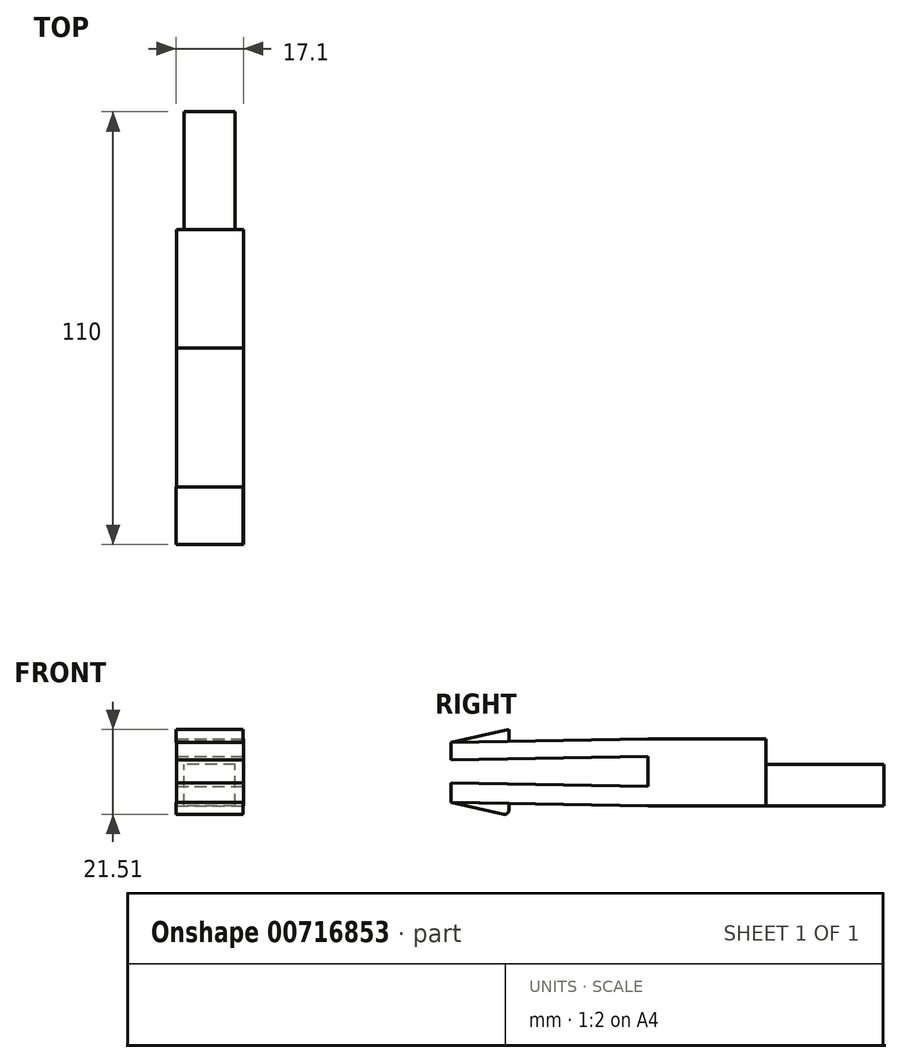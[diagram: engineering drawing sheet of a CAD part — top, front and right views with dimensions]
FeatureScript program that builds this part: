
annotation { "Feature Type Name" : "Feature", "Feature Type Description" : "" }
export const myFeature = defineFeature(function(context is Context, id is Id, definition is map)
    precondition{}
    {
        {
            var Q0;
            Q0=qCreatedBy(makeId("Front.planeOp"),FACE);
            var sketch = newSketch(context, id + "F0", { "sketchPlane" : qUnion([Q0])});
            skLineSegment(sketch, "E0.bottom", {"start": v(6.5, -5.25) * mm, "end": v(-6.5, -5.25) * mm});
            skLineSegment(sketch, "E0.top", {"start": v(6.5, 5.25) * mm, "end": v(-6.5, 5.25) * mm});
            skLineSegment(sketch, "E0.left", {"start": v(6.5, -5.25) * mm, "end": v(6.5, 5.25) * mm});
            skLineSegment(sketch, "E0.right", {"start": v(-6.5, -5.25) * mm, "end": v(-6.5, 5.25) * mm});
            skPoint(sketch, "E0.middle", {"position": v(0, 0) * mm});
            skSolve(sketch);
        }
        {
            var Q0;
            Q0 = qSketchRegion(id + "F0", true);
            extrude(context, id + "F1", {"entities" : qUnion([Q0]), "oppositeDirection" : true, "depth" : 30 * mm, "offsetDistance" : 25 * mm});
        }
        {
            var Q0;
            Q0=makeQuery(id+"F1.opExtrude","CAP_FACE",FACE,{"disambiguationData":[OSD([sQuery(id+"F0.wireOp",EDGE,"E0.bottom"),sQuery(id+"F0.wireOp",EDGE,"E0.top"),sQuery(id+"F0.wireOp",EDGE,"E0.left"),sQuery(id+"F0.wireOp",EDGE,"E0.right")])],"isStart":true});
            var sketch = newSketch(context, id + "F2", { "sketchPlane" : qUnion([Q0])});
            skLineSegment(sketch, "E1.bottom", {"start": v(-8.4, 11.75) * mm, "end": v(8.6, 11.75) * mm});
            skLineSegment(sketch, "E1.top", {"start": v(-8.4, -5.25) * mm, "end": v(8.6, -5.25) * mm});
            skLineSegment(sketch, "E1.left", {"start": v(-8.4, 11.75) * mm, "end": v(-8.4, -5.25) * mm});
            skLineSegment(sketch, "E1.right", {"start": v(8.6, 11.75) * mm, "end": v(8.6, -5.25) * mm});
            skSolve(sketch);
        }
        {
            var Q0;
            Q0=makeQuery(id+"F2.imprint","IMPRINT",FACE,{"disambiguationData":[TD([[makeQuery(id+"F2.imprint","IMPRINT",EDGE,{"derivedFrom":sQuery(id+"F2.wireOp",EDGE,"E1.bottom")}),-1.0]])]});
            var Q1;
            Q1=makeQuery(id+"F2.imprint","IMPRINT",FACE,{"disambiguationData":[TD([[makeQuery(id+"F2.imprint","IMPRINT",EDGE,{"derivedFrom":makeQuery(id+"F1.opExtrude","CAP_EDGE",EDGE,{"disambiguationData":[OSD([sQuery(id+"F0.wireOp",EDGE,"E0.top")])],"isStart":true})}),1.0]])]});
            extrude(context, id + "F3", {"entities" : qUnion([Q0, Q1]), "operationType" : NewBodyOperationType.ADD, "depth" : 30 * mm, "offsetDistance" : 25 * mm});
        }
        {
            var Q0;
            Q0=makeQuery(id+"F3.opExtrude","CAP_FACE",FACE,{"disambiguationData":[OSD([sQuery(id+"F2.wireOp",EDGE,"E1.bottom"),sQuery(id+"F2.wireOp",EDGE,"E1.top"),sQuery(id+"F2.wireOp",EDGE,"E1.left"),sQuery(id+"F2.wireOp",EDGE,"E1.right")])],"isStart":false});
            var sketch = newSketch(context, id + "F4", { "sketchPlane" : qUnion([Q0])});
            skLineSegment(sketch, "E2.bottom", {"start": v(-8.4, 11.75) * mm, "end": v(8.6, 11.75) * mm});
            skLineSegment(sketch, "E2.top", {"start": v(-8.4, 7.32) * mm, "end": v(8.6, 7.32) * mm});
            skLineSegment(sketch, "E2.left", {"start": v(-8.4, 11.75) * mm, "end": v(-8.4, 7.32) * mm});
            skLineSegment(sketch, "E2.right", {"start": v(8.6, 11.75) * mm, "end": v(8.6, 7.32) * mm});
            skLineSegment(sketch, "E3.bottom", {"start": v(-8.4, -5.25) * mm, "end": v(8.6, -5.25) * mm});
            skLineSegment(sketch, "E3.top", {"start": v(-8.4, -0.25) * mm, "end": v(8.6, -0.25) * mm});
            skLineSegment(sketch, "E3.left", {"start": v(-8.4, -5.25) * mm, "end": v(-8.4, -0.25) * mm});
            skLineSegment(sketch, "E3.right", {"start": v(8.6, -5.25) * mm, "end": v(8.6, -0.25) * mm});
            skSolve(sketch);
        }
        {
            var Q0;
            Q0=makeQuery(id+"F3.opExtrude","SWEPT_FACE",FACE,{"disambiguationData":[OSD([sQuery(id+"F2.wireOp",EDGE,"E1.right")])]});
            var sketch = newSketch(context, id + "F5", { "sketchPlane" : qUnion([Q0])});
            skLineSegment(sketch, "E4", {"start": v(-30, 9.54) * mm, "end": v(-80, 8.67) * mm});
            skLineSegment(sketch, "E5", {"start": v(-30, -2.92) * mm, "end": v(-80, -2.04) * mm});
            skSolve(sketch);
        }
        {
            var Q0;
            Q0=makeQuery(id+"F4.imprint","IMPRINT",FACE,{"disambiguationData":[TD([[makeQuery(id+"F4.imprint","IMPRINT",EDGE,{"derivedFrom":sQuery(id+"F4.wireOp",EDGE,"E2.bottom")}),-1.0]])]});
            var Q1;
            Q1=sQuery(id+"F5.wireOp",EDGE,"E4");
            sweep(context, id + "F6", {"operationType" : NewBodyOperationType.ADD, "profiles" : qUnion([Q0]), "path" : qUnion([Q1])});
        }
        {
            var Q0;
            Q0=makeQuery(id+"F4.imprint","IMPRINT",FACE,{"disambiguationData":[TD([[makeQuery(id+"F4.imprint","IMPRINT",EDGE,{"derivedFrom":sQuery(id+"F4.wireOp",EDGE,"E3.bottom")}),1.0]])]});
            var Q1;
            Q1=sQuery(id+"F5.wireOp",EDGE,"E5");
            sweep(context, id + "F7", {"operationType" : NewBodyOperationType.ADD, "profiles" : qUnion([Q0]), "path" : qUnion([Q1])});
        }
        {
            var Q0;
            Q0=qCreatedBy(makeId("Right.planeOp"),FACE);
            var sketch = newSketch(context, id + "F8", { "sketchPlane" : qUnion([Q0])});
            skLineSegment(sketch, "E6", {"start": v(-80, 10.88) * mm, "end": v(-65.35, 14.13) * mm});
            skLineSegment(sketch, "E7", {"start": v(-65.35, 14.13) * mm, "end": v(-65.35, 11.13) * mm});
            skLineSegment(sketch, "E8", {"start": v(-65.35, 11.13) * mm, "end": v(-80, 10.88) * mm});
            skLineSegment(sketch, "E9", {"start": v(-80, -4.38) * mm, "end": v(-65.35, -7.63) * mm});
            skLineSegment(sketch, "E10", {"start": v(-65.35, -7.63) * mm, "end": v(-65.35, -4.63) * mm});
            skLineSegment(sketch, "E11", {"start": v(-65.35, -4.63) * mm, "end": v(-80, -4.38) * mm});
            skSolve(sketch);
        }
        {
            var Q0;
            Q0 = qSketchRegion(id + "F8", true);
            extrude(context, id + "F9", {"entities" : qUnion([Q0]), "operationType" : NewBodyOperationType.ADD, "depth" : 8.5 * mm, "offsetDistance" : 25 * mm, "hasSecondDirection" : true, "secondDirectionOppositeDirection" : true, "secondDirectionDepth" : 8.5 * mm});
        }
        {
            var Q0;
            Q0=makeQuery(id+"F9.opExtrude","SWEPT_EDGE",EDGE,{"disambiguationData":[OSD([sQuery(id+"F8.wireOp",EDGE,"E6"),sQuery(id+"F8.wireOp",EDGE,"E7")])]});
            var Q1;
            Q1=makeQuery(id+"F9.boolean.opBoolean","MERGE",EDGE,{"derivedFrom":[makeQuery(id+"F6.opSweep","CAP_EDGE",EDGE,{"disambiguationData":[OSD([sQuery(id+"F4.wireOp",EDGE,"E2.bottom"),sQuery(id+"F5.wireOp",VERTEX,"E4.end")])],"isStart":false}),makeQuery(id+"F9.opExtrude","SWEPT_EDGE",EDGE,{"disambiguationData":[OSD([sQuery(id+"F8.wireOp",EDGE,"E6"),sQuery(id+"F8.wireOp",EDGE,"E8")])]})]});
            var Q2;
            Q2=makeQuery(id+"F3.opExtrude","CAP_EDGE",EDGE,{"disambiguationData":[OSD([sQuery(id+"F2.wireOp",EDGE,"E1.bottom")])],"isStart":true});
            var Q3;
            Q3=makeQuery(id+"F3.opExtrude","CAP_EDGE",EDGE,{"disambiguationData":[OSD([sQuery(id+"F2.wireOp",EDGE,"E1.right")])],"isStart":true});
            var Q4;
            Q4=makeQuery(id+"F3.opExtrude","CAP_EDGE",EDGE,{"disambiguationData":[OSD([sQuery(id+"F2.wireOp",EDGE,"E1.left")])],"isStart":true});
            var Q5;
            Q5=makeQuery(id+"F1.opExtrude","CAP_EDGE",EDGE,{"disambiguationData":[OSD([sQuery(id+"F0.wireOp",EDGE,"E0.right")])],"isStart":false});
            var Q6;
            Q6=makeQuery(id+"F1.opExtrude","CAP_EDGE",EDGE,{"disambiguationData":[OSD([sQuery(id+"F0.wireOp",EDGE,"E0.top")])],"isStart":false});
            var Q7;
            Q7=makeQuery(id+"F1.opExtrude","CAP_EDGE",EDGE,{"disambiguationData":[OSD([sQuery(id+"F0.wireOp",EDGE,"E0.bottom")])],"isStart":false});
            var Q8;
            Q8=makeQuery(id+"F1.opExtrude","CAP_EDGE",EDGE,{"disambiguationData":[OSD([sQuery(id+"F0.wireOp",EDGE,"E0.left")])],"isStart":false});
            var Q9;
            Q9=makeQuery(id+"F9.opExtrude","SWEPT_EDGE",EDGE,{"disambiguationData":[OSD([sQuery(id+"F8.wireOp",EDGE,"E9"),sQuery(id+"F8.wireOp",EDGE,"E10")])]});
            var Q10;
            Q10=makeQuery(id+"F9.boolean.opBoolean","MERGE",EDGE,{"derivedFrom":[makeQuery(id+"F7.opSweep","CAP_EDGE",EDGE,{"disambiguationData":[OSD([sQuery(id+"F4.wireOp",EDGE,"E3.bottom"),sQuery(id+"F5.wireOp",VERTEX,"E5.end")])],"isStart":false}),makeQuery(id+"F9.opExtrude","SWEPT_EDGE",EDGE,{"disambiguationData":[OSD([sQuery(id+"F8.wireOp",EDGE,"E9"),sQuery(id+"F8.wireOp",EDGE,"E11")])]})]});
            var Q11;
            Q11=makeQuery(id+"F6.opSweep","CAP_EDGE",EDGE,{"disambiguationData":[OSD([sQuery(id+"F4.wireOp",EDGE,"E2.top"),sQuery(id+"F5.wireOp",VERTEX,"E4.end")])],"isStart":false});
            var Q12;
            Q12=makeQuery(id+"F7.opSweep","CAP_EDGE",EDGE,{"disambiguationData":[OSD([sQuery(id+"F4.wireOp",EDGE,"E3.top"),sQuery(id+"F5.wireOp",VERTEX,"E5.end")])],"isStart":false});
            fillet(context, id + "F10", {"entities" : qUnion([Q0, Q1, Q2, Q3, Q4, Q5, Q6, Q7, Q8, Q9, Q10, Q11, Q12]), "radius" : 1 * mm, "tangentPropagation" : true, "allowEdgeOverflow" : false});
        }
    });
